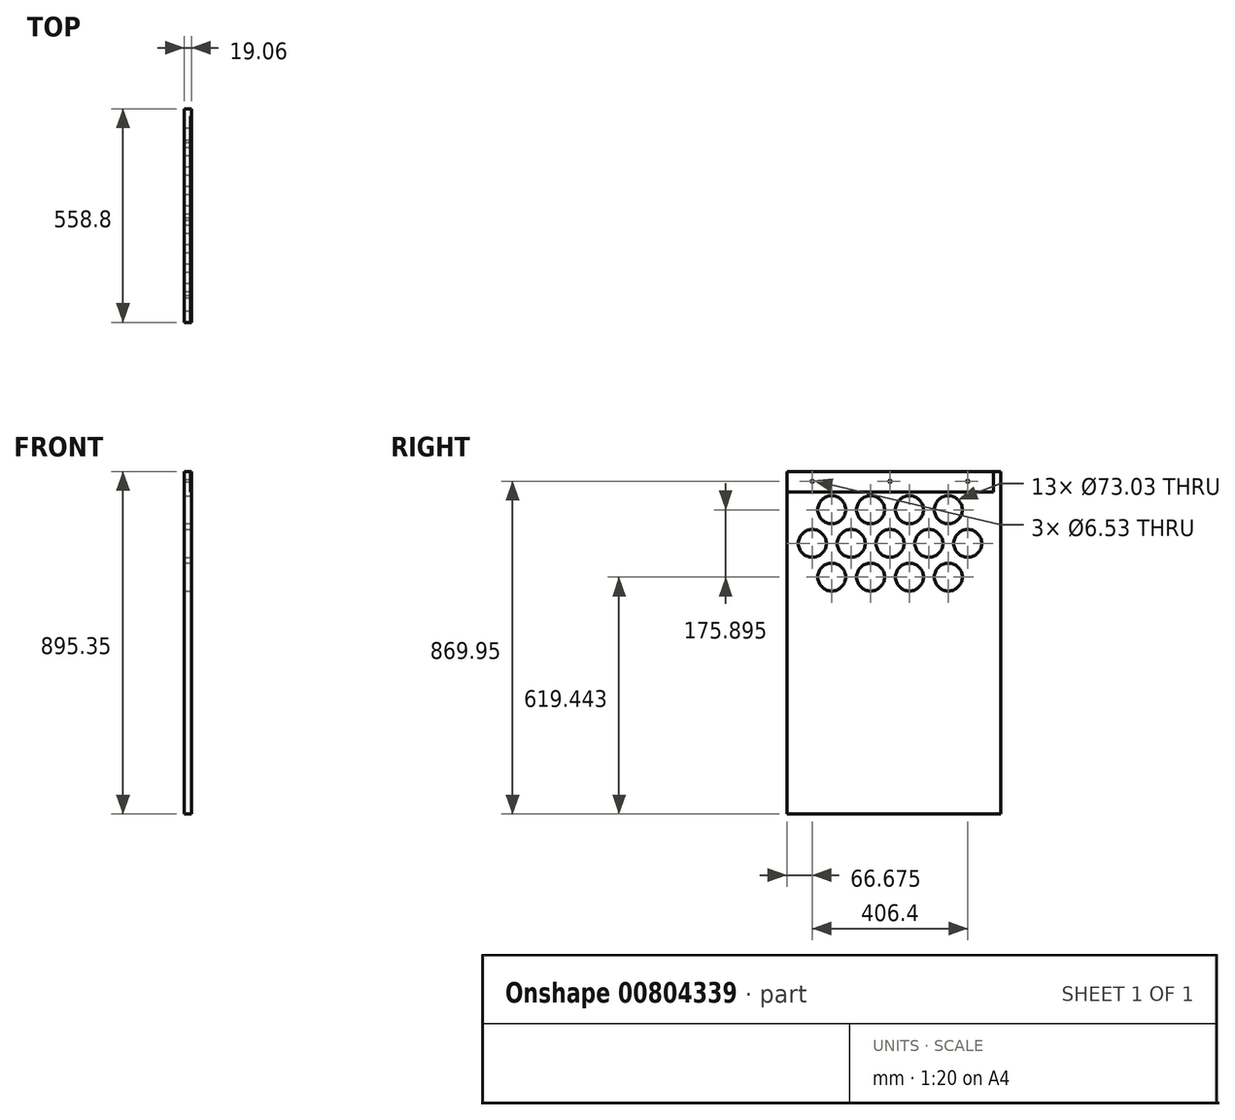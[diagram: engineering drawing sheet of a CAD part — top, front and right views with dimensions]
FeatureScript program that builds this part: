
annotation { "Feature Type Name" : "Feature", "Feature Type Description" : "" }
export const myFeature = defineFeature(function(context is Context, id is Id, definition is map)
    precondition{}
    {
        {
            var Q0;
            Q0=qCreatedBy(makeId("Front.planeOp"),FACE);
            var sketch = newSketch(context, id + "F0", { "sketchPlane" : qUnion([Q0])});
            skLineSegment(sketch, "E0.bottom", {"start": v(9.52, -168.91) * mm, "end": v(-9.53, -168.91) * mm});
            skLineSegment(sketch, "E0.top", {"start": v(9.53, 168.91) * mm, "end": v(-9.53, 168.91) * mm});
            skLineSegment(sketch, "E0.left", {"start": v(9.52, -168.91) * mm, "end": v(9.53, 168.91) * mm});
            skLineSegment(sketch, "E0.right", {"start": v(-9.53, -168.91) * mm, "end": v(-9.53, 168.91) * mm});
            skPoint(sketch, "E0.middle", {"position": v(0, 0) * mm});
            skSolve(sketch);
        }
        {
            var Q0;
            Q0=makeQuery(id+"F0.imprint","IMPRINT",FACE,{"disambiguationData":[TD([[makeQuery(id+"F0.imprint","IMPRINT",EDGE,{"derivedFrom":sQuery(id+"F0.wireOp",EDGE,"E0.bottom")}),-1.0]])]});
            extrude(context, id + "F1", {"entities" : qUnion([Q0]), "depth" : 539.75 * mm, "offsetDistance" : 25.4 * mm});
        }
        {
            var Q0;
            Q0=makeQuery(id+"F1.opExtrude","SWEPT_FACE",FACE,{"disambiguationData":[OSD([sQuery(id+"F0.wireOp",EDGE,"E0.left")])]});
            var sketch = newSketch(context, id + "F2", { "sketchPlane" : qUnion([Q0])});
            skLineSegment(sketch, "E1", {"start": v(-269.88, 130.8) * mm, "end": v(-269.88, -168.9) * mm, "construction": true});
            skCircle(sketch, "E2", {"center": v(-269.88, -19.05) * mm, "radius": 36.51 * mm});
            skLineSegment(sketch, "E3", {"start": v(-269.88, -19.05) * mm, "end": v(-371.43, -19.05) * mm, "construction": true});
            skLineSegment(sketch, "E4", {"start": v(-371.43, -19.05) * mm, "end": v(-320.65, 68.9) * mm, "construction": true});
            skLineSegment(sketch, "E5", {"start": v(-320.65, 68.9) * mm, "end": v(-269.88, -19.05) * mm, "construction": true});
            skCircle(sketch, "E6", {"center": v(-320.65, 68.9) * mm, "radius": 36.51 * mm});
            skCircle(sketch, "E7.1.0.0", {"center": v(-219.05, 68.9) * mm, "radius": 36.51 * mm});
            skCircle(sketch, "E7.1.0.1", {"center": v(-168.28, -19.05) * mm, "radius": 36.51 * mm});
            skCircle(sketch, "E7.2.0.0", {"center": v(-117.45, 68.9) * mm, "radius": 36.51 * mm});
            skCircle(sketch, "E7.2.0.1", {"center": v(-66.67, -19.05) * mm, "radius": 36.51 * mm});
            skLineSegment(sketch, "E7.direction1", {"start": v(-320.65, 68.9) * mm, "end": v(-219.05, 68.9) * mm, "construction": true});
            skCircle(sketch, "E8.MirrorC", {"center": v(-371.48, -19.05) * mm, "radius": 36.51 * mm});
            skCircle(sketch, "E9.MirrorC", {"center": v(-422.3, 68.9) * mm, "radius": 36.51 * mm});
            skCircle(sketch, "E10.MirrorC", {"center": v(-473.08, -19.05) * mm, "radius": 36.51 * mm});
            skCircle(sketch, "E11.MirrorC", {"center": v(-422.3, -107) * mm, "radius": 36.51 * mm});
            skCircle(sketch, "E12.MirrorC", {"center": v(-320.65, -107) * mm, "radius": 36.51 * mm});
            skCircle(sketch, "E13.MirrorC", {"center": v(-219.05, -107) * mm, "radius": 36.51 * mm});
            skCircle(sketch, "E14.MirrorC", {"center": v(-117.45, -107) * mm, "radius": 36.51 * mm});
            skLineSegment(sketch, "E15", {"start": v(-269.88, 130.8) * mm, "end": v(-269.88, 168.91) * mm, "construction": true});
            skSolve(sketch);
        }
        {
            var Q0;
            Q0=qSketchRegion(id+"F2",true);
            extrude(context, id + "F3", {"entities" : qUnion([Q0]), "operationType" : NewBodyOperationType.REMOVE, "oppositeDirection" : true, "depth" : 25.4 * mm, "offsetDistance" : 25.4 * mm});
        }
        {
            var Q0;
            Q0=makeQuery(id+"F1.opExtrude","SWEPT_FACE",FACE,{"disambiguationData":[OSD([sQuery(id+"F0.wireOp",EDGE,"E0.bottom")])]});
            extrude(context, id + "F4", {"entities" : qUnion([Q0]), "operationType" : NewBodyOperationType.ADD, "depth" : 557.53 * mm, "offsetDistance" : 25.4 * mm});
        }
        {
            var Q0;
            {var subQ0=sQuery(id+"F0.wireOp",EDGE,"E0.bottom");Q0=makeQuery(id+"F4.boolean.opBoolean","MERGE",FACE,{"derivedFrom":[makeQuery(id+"F1.opExtrude","CAP_FACE",FACE,{"disambiguationData":[OSD([subQ0,sQuery(id+"F0.wireOp",EDGE,"E0.top"),sQuery(id+"F0.wireOp",EDGE,"E0.left"),sQuery(id+"F0.wireOp",EDGE,"E0.right")])],"isStart":true}),makeQuery(id+"F4.opExtrude","SWEPT_FACE",FACE,{"disambiguationData":[OSD([subQ0]),TDD([makeQuery(id+"F1.opExtrude","CAP_EDGE",EDGE,{"disambiguationData":[OSD([subQ0])],"isStart":true})])]})]});}
            extrude(context, id + "F5", {"entities" : qUnion([Q0]), "operationType" : NewBodyOperationType.ADD, "depth" : 19.05 * mm, "offsetDistance" : 25.4 * mm});
        }
        {
            var Q0;
            {var subQ0=sQuery(id+"F0.wireOp",EDGE,"E0.bottom");Q0=makeQuery(id+"F4.boolean.opBoolean","MERGE",FACE,{"derivedFrom":[makeQuery(id+"F1.opExtrude","CAP_FACE",FACE,{"disambiguationData":[OSD([subQ0,sQuery(id+"F0.wireOp",EDGE,"E0.top"),sQuery(id+"F0.wireOp",EDGE,"E0.left"),sQuery(id+"F0.wireOp",EDGE,"E0.right")])],"isStart":false}),makeQuery(id+"F4.opExtrude","SWEPT_FACE",FACE,{"disambiguationData":[OSD([subQ0]),TDD([makeQuery(id+"F1.opExtrude","CAP_EDGE",EDGE,{"disambiguationData":[OSD([subQ0])],"isStart":false})])]})]});}
            var sketch = newSketch(context, id + "F6", { "sketchPlane" : qUnion([Q0])});
            skLineSegment(sketch, "E16.bottom", {"start": v(6.35, 168.91) * mm, "end": v(9.53, 168.91) * mm});
            skLineSegment(sketch, "E16.top", {"start": v(6.35, 114.94) * mm, "end": v(9.53, 114.94) * mm});
            skLineSegment(sketch, "E16.left", {"start": v(6.35, 168.91) * mm, "end": v(6.35, 114.94) * mm});
            skLineSegment(sketch, "E16.right", {"start": v(9.53, 168.91) * mm, "end": v(9.53, 114.94) * mm});
            skSolve(sketch);
        }
        {
            var Q0;
            Q0 = qSketchRegion(id + "F6", true);
            var Q1;
            Q1=makeQuery(id+"F5.opExtrude","CAP_FACE",FACE,{"disambiguationData":[OSD([sQuery(id+"F0.wireOp",EDGE,"E0.bottom"),sQuery(id+"F0.wireOp",EDGE,"E0.top"),sQuery(id+"F0.wireOp",EDGE,"E0.left"),sQuery(id+"F0.wireOp",EDGE,"E0.right")])],"isStart":false});
            extrude(context, id + "F7", {"entities" : qUnion([Q0]), "operationType" : NewBodyOperationType.REMOVE, "endBound" : BoundingType.UP_TO_SURFACE, "oppositeDirection" : true, "depth" : 25.4 * mm, "endBoundEntityFace" : qUnion([Q1]), "hasOffset" : true, "offsetDistance" : 19.05 * mm});
        }
        {
            var Q0;
            {var subQ0=sQuery(id+"F0.wireOp",EDGE,"E0.right");var subQ1=sQuery(id+"F0.wireOp",EDGE,"E0.bottom");Q0=makeQuery(id+"F5.boolean.opBoolean","MERGE",FACE,{"derivedFrom":[makeQuery(id+"F4.boolean.opBoolean","MERGE",FACE,{"derivedFrom":[makeQuery(id+"F1.opExtrude","SWEPT_FACE",FACE,{"disambiguationData":[OSD([subQ0])]}),makeQuery(id+"F4.opExtrude","SWEPT_FACE",FACE,{"disambiguationData":[OSD([subQ1,subQ0])]})]}),makeQuery(id+"F5.opExtrude","SWEPT_FACE",FACE,{"disambiguationData":[OSD([subQ1,subQ0])]})]});}
            var sketch = newSketch(context, id + "F8", { "sketchPlane" : qUnion([Q0])});
            skLineSegment(sketch, "E17", {"start": v(269.88, -19.05) * mm, "end": v(269.88, 168.91) * mm, "construction": true});
            skLineSegment(sketch, "E18", {"start": v(473.08, -19.05) * mm, "end": v(473.08, 168.91) * mm, "construction": true});
            skLineSegment(sketch, "E19", {"start": v(269.88, 143.51) * mm, "end": v(473.08, 143.51) * mm, "construction": true});
            skPoint(sketch, "E20", {"position": v(269.88, 143.51) * mm});
            skPoint(sketch, "E21", {"position": v(473.08, 143.51) * mm});
            skPoint(sketch, "E22.MirrorP", {"position": v(66.67, 143.51) * mm});
            skLineSegment(sketch, "E23", {"start": v(539.75, -168.9) * mm, "end": v(-19.05, -168.91) * mm, "construction": true});
            skLineSegment(sketch, "E24.0", {"start": v(539.75, -178.44) * mm, "end": v(-19.05, -178.44) * mm, "construction": true});
            skLineSegment(sketch, "E25", {"start": v(371.48, 143.51) * mm, "end": v(371.48, -178.44) * mm, "construction": true});
            skLineSegment(sketch, "E26", {"start": v(371.48, -17.46) * mm, "end": v(539.75, -17.46) * mm, "construction": true});
            skSolve(sketch);
        }
        {
            var Q0;
            Q0=sQuery(id+"F8.wireOp",VERTEX,"E22.MirrorP");
            var Q1;
            Q1=sQuery(id+"F8.wireOp",VERTEX,"E20");
            var Q2;
            Q2=sQuery(id+"F8.wireOp",VERTEX,"E21");
            var Q3;
            Q3=sQuery(id+"F8.wireOp",VERTEX,"57911b12-5905-4055-b7ee-9814e1e721e10.MirrorP");
            var Q4;
            Q4=sQuery(id+"F8.wireOp",VERTEX,"aec2a50c-7c24-43c6-951b-707cfa8967cd0.MirrorP");
            var Q5;
            Q5=sQuery(id+"F8.wireOp",VERTEX,"32984d8b-0f13-4f81-af50-a6bc22765dd30.MirrorP");
            var Q6;
            Q6=makeQuery(id+"F1.opExtrude","SWEPT_BODY",BODY,{"disambiguationData":[OSD([sQuery(id+"F0.wireOp",EDGE,"E0.bottom"),sQuery(id+"F0.wireOp",EDGE,"E0.top"),sQuery(id+"F0.wireOp",EDGE,"E0.left"),sQuery(id+"F0.wireOp",EDGE,"E0.right")])]});
            hole(context, id + "F9", {"style" : HoleStyle.SIMPLE, "endStyle" : HoleEndStyle.THROUGH, "standardTappedOrClearance" : lookupTablePath({ "standard" : "ANSI", "fit" : "Close", "size" : "1/4", "type" : "Clearance" }), "standardBlindInLast" : lookupTablePath({ "fit" : "Close", "standard" : "ANSI", "size" : "1/4", "type" : "Clearance" }), "holeDiameter" : 6.53 * mm, "majorDiameter" : 6.35 * mm, "isTappedThrough" : true, "tappedDepth" : 12.7 * mm, "tapClearance" : 3, "startFromSketch" : true, "locations" : qUnion([Q0, Q1, Q2, Q3, Q4, Q5]), "scope" : qUnion([Q6])});
        }
    });
